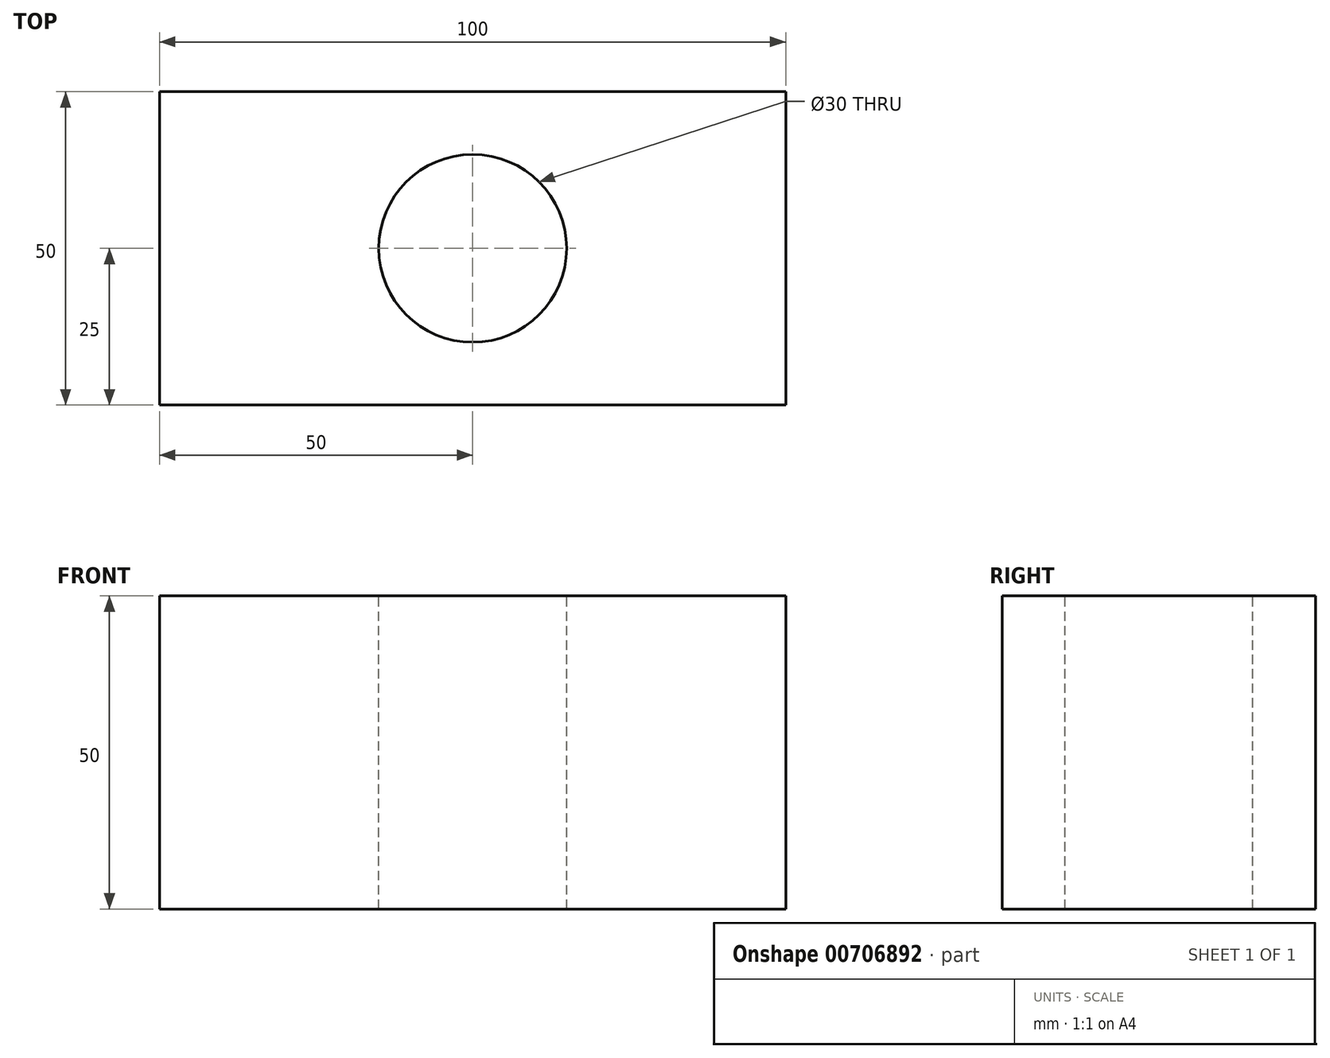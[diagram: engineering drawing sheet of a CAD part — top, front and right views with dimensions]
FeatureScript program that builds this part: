
annotation { "Feature Type Name" : "Feature", "Feature Type Description" : "" }
export const myFeature = defineFeature(function(context is Context, id is Id, definition is map)
    precondition{}
    {
        {
            var Q0;
            Q0=qCreatedBy(makeId("Top.planeOp"),FACE);
            var sketch = newSketch(context, id + "F0", { "sketchPlane" : qUnion([Q0])});
            skLineSegment(sketch, "E0.bottom", {"start": v(-50, -25) * mm, "end": v(50, -25) * mm});
            skLineSegment(sketch, "E0.top", {"start": v(-50, 25) * mm, "end": v(50, 25) * mm});
            skLineSegment(sketch, "E0.left", {"start": v(-50, -25) * mm, "end": v(-50, 25) * mm});
            skLineSegment(sketch, "E0.right", {"start": v(50, -25) * mm, "end": v(50, 25) * mm});
            skSolve(sketch);
        }
        {
            var Q0;
            Q0=makeQuery(id+"F0.imprint","IMPRINT",FACE,{"disambiguationData":[TD([[makeQuery(id+"F0.imprint","IMPRINT",EDGE,{"derivedFrom":sQuery(id+"F0.wireOp",EDGE,"E0.bottom")}),1.0]])]});
            extrude(context, id + "F1", {"entities" : qUnion([Q0]), "depth" : 50 * mm, "offsetDistance" : 25 * mm});
        }
        {
            var Q0;
            Q0=makeQuery(id+"F1.opExtrude","CAP_FACE",FACE,{"disambiguationData":[OSD([sQuery(id+"F0.wireOp",EDGE,"E0.bottom"),sQuery(id+"F0.wireOp",EDGE,"E0.top"),sQuery(id+"F0.wireOp",EDGE,"E0.left"),sQuery(id+"F0.wireOp",EDGE,"E0.right")])],"isStart":false});
            var sketch = newSketch(context, id + "F2", { "sketchPlane" : qUnion([Q0])});
            skCircle(sketch, "E1", {"center": v(0, 0) * mm, "radius": 15 * mm});
            skSolve(sketch);
        }
        {
            var Q0;
            Q0=makeQuery(id+"F2.imprint","IMPRINT",FACE,{"disambiguationData":[TD([[makeQuery(id+"F2.imprint","IMPRINT",EDGE,{"derivedFrom":sQuery(id+"F2.wireOp",EDGE,"E1")}),1.0]])]});
            extrude(context, id + "F3", {"entities" : qUnion([Q0]), "operationType" : NewBodyOperationType.REMOVE, "oppositeDirection" : true, "depth" : -50 * mm, "offsetDistance" : 25 * mm});
        }
        {
            var Q0;
            Q0=makeQuery(id+"F2.imprint","IMPRINT",FACE,{"disambiguationData":[TD([[makeQuery(id+"F2.imprint","IMPRINT",EDGE,{"derivedFrom":sQuery(id+"F2.wireOp",EDGE,"E1")}),1.0]])]});
            extrude(context, id + "F4", {"entities" : qUnion([Q0]), "operationType" : NewBodyOperationType.REMOVE, "oppositeDirection" : true, "depth" : 50 * mm, "offsetDistance" : 25 * mm});
        }
    });
